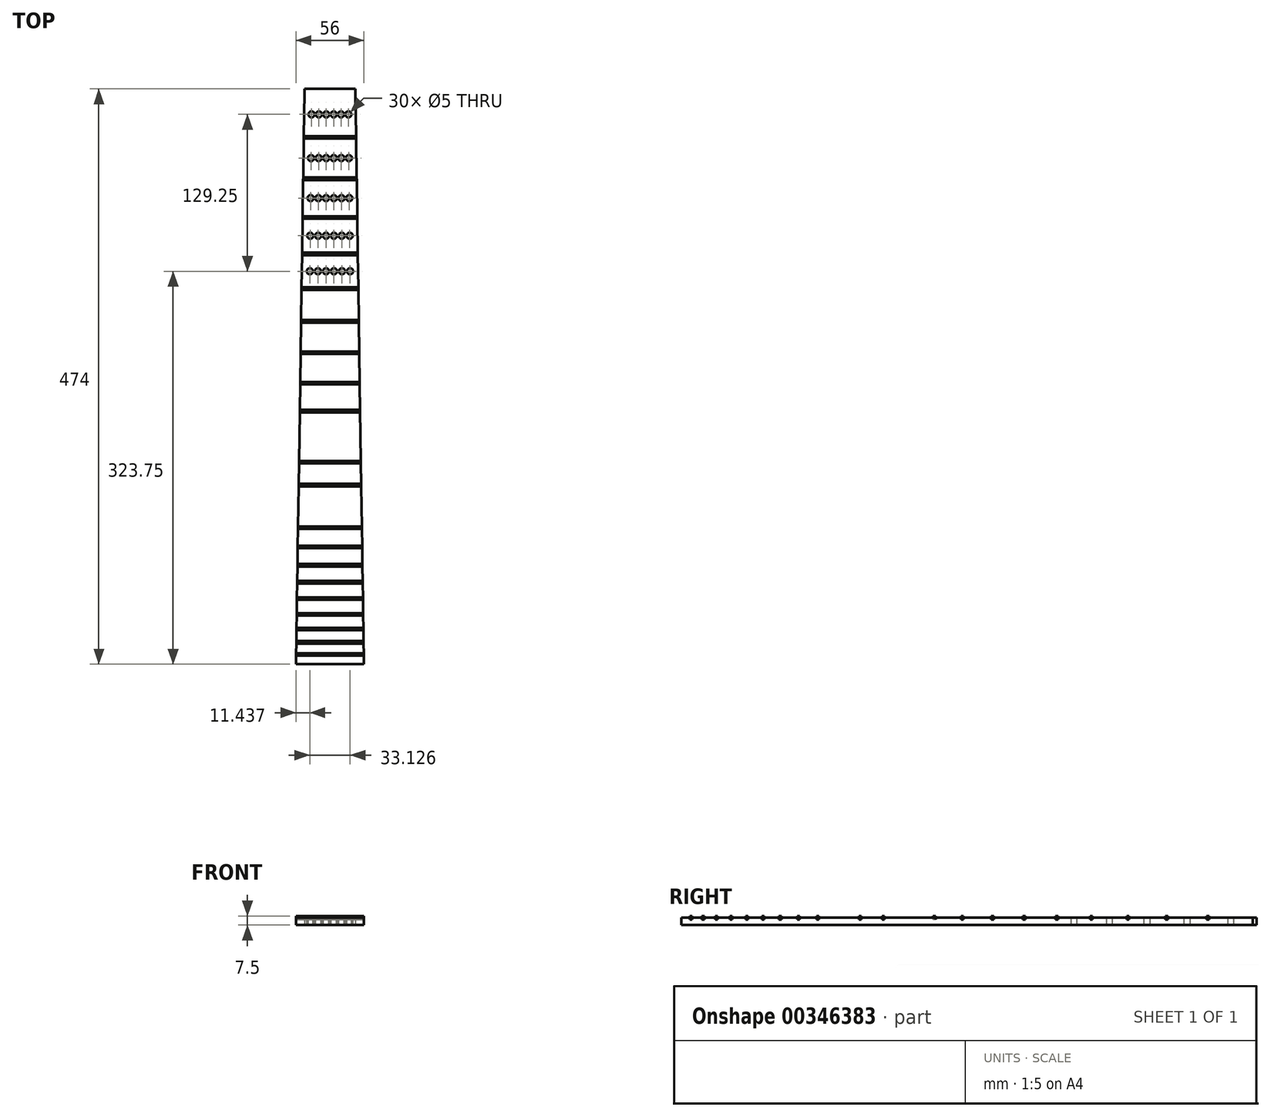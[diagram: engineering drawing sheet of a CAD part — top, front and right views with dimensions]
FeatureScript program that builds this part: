
annotation { "Feature Type Name" : "Feature", "Feature Type Description" : "" }
export const myFeature = defineFeature(function(context is Context, id is Id, definition is map)
    precondition{}
    {
        {
            var Q0;
            Q0=qCreatedBy(makeId("Top.planeOp"),FACE);
            var sketch = newSketch(context, id + "F0", { "sketchPlane" : qUnion([Q0])});
            skLineSegment(sketch, "E0", {"start": v(0, 0) * mm, "end": v(0, 471) * mm, "construction": true});
            skLineSegment(sketch, "E1", {"start": v(0, 471) * mm, "end": v(-21, 471) * mm});
            skLineSegment(sketch, "E2", {"start": v(-28, 0) * mm, "end": v(0, 0) * mm});
            skLineSegment(sketch, "E3", {"start": v(-21, 471) * mm, "end": v(-28, 0) * mm});
            skLineSegment(sketch, "E4.MirrorCS", {"start": v(0, 471) * mm, "end": v(21, 471) * mm});
            skLineSegment(sketch, "E5.MirrorCS", {"start": v(21, 471) * mm, "end": v(28, 0) * mm});
            skLineSegment(sketch, "E6.MirrorCS", {"start": v(28, 0) * mm, "end": v(0, 0) * mm});
            skLineSegment(sketch, "E7", {"start": v(-21, 471) * mm, "end": v(21, 471) * mm, "construction": true});
            skLineSegment(sketch, "E8", {"start": v(-21, 471) * mm, "end": v(-21, 474) * mm});
            skLineSegment(sketch, "E9", {"start": v(21, 471) * mm, "end": v(21, 474) * mm});
            skLineSegment(sketch, "E10", {"start": v(-21, 474) * mm, "end": v(21, 474) * mm});
            skSolve(sketch);
        }
        {
            var Q0;
            Q0 = qSketchRegion(id + "F0", true);
            extrude(context, id + "F1", {"entities" : qUnion([Q0]), "depth" : 6 * mm});
        }
        {
            var Q0;
            Q0=makeQuery(id+"F1.opExtrude","CAP_FACE",FACE,{"disambiguationData":[OSD([sQuery(id+"F0.wireOp",EDGE,"E1"),sQuery(id+"F0.wireOp",EDGE,"E2"),sQuery(id+"F0.wireOp",EDGE,"E3"),sQuery(id+"F0.wireOp",EDGE,"E4.MirrorCS"),sQuery(id+"F0.wireOp",EDGE,"E5.MirrorCS"),sQuery(id+"F0.wireOp",EDGE,"E6.MirrorCS")])],"isStart":false});
            var sketch = newSketch(context, id + "F2", { "sketchPlane" : qUnion([Q0])});
            skLineSegment(sketch, "E11", {"start": v(-21.54, 435) * mm, "end": v(21.54, 435) * mm});
            skLineSegment(sketch, "E12", {"start": v(-21.56, 433) * mm, "end": v(21.56, 433) * mm});
            skLineSegment(sketch, "E13", {"start": v(-22.04, 401) * mm, "end": v(22.04, 401) * mm});
            skLineSegment(sketch, "E14", {"start": v(-22.07, 399) * mm, "end": v(22.07, 399) * mm});
            skLineSegment(sketch, "E15", {"start": v(-22.52, 369) * mm, "end": v(22.52, 369) * mm});
            skLineSegment(sketch, "E16", {"start": v(-22.55, 367) * mm, "end": v(22.55, 367) * mm});
            skLineSegment(sketch, "E17", {"start": v(-22.96, 339) * mm, "end": v(22.96, 339) * mm});
            skLineSegment(sketch, "E18", {"start": v(-23, 337) * mm, "end": v(23, 337) * mm});
            skLineSegment(sketch, "E19", {"start": v(-23.39, 310.5) * mm, "end": v(23.39, 310.5) * mm});
            skLineSegment(sketch, "E20", {"start": v(-23.42, 308.5) * mm, "end": v(23.42, 308.5) * mm});
            skLineSegment(sketch, "E21", {"start": v(-23.79, 283.5) * mm, "end": v(23.79, 283.5) * mm});
            skLineSegment(sketch, "E22", {"start": v(-23.82, 281.5) * mm, "end": v(23.82, 281.5) * mm});
            skLineSegment(sketch, "E23", {"start": v(-24.17, 257.5) * mm, "end": v(24.17, 257.5) * mm});
            skLineSegment(sketch, "E24", {"start": v(-24.2, 255.5) * mm, "end": v(24.2, 255.5) * mm});
            skLineSegment(sketch, "E25", {"start": v(-24.54, 232.5) * mm, "end": v(24.54, 232.5) * mm});
            skLineSegment(sketch, "E26", {"start": v(-24.57, 230.5) * mm, "end": v(24.57, 230.5) * mm});
            skLineSegment(sketch, "E27", {"start": v(-24.89, 209.5) * mm, "end": v(24.89, 209.5) * mm});
            skLineSegment(sketch, "E28", {"start": v(-24.92, 207.5) * mm, "end": v(24.89, 207.5) * mm});
            skLineSegment(sketch, "E29", {"start": v(-25.21, 187.5) * mm, "end": v(25.21, 187.5) * mm});
            skLineSegment(sketch, "E30", {"start": v(-25.24, 185.5) * mm, "end": v(25.21, 185.5) * mm});
            skLineSegment(sketch, "E31", {"start": v(-25.51, 167.5) * mm, "end": v(25.51, 167.5) * mm});
            skLineSegment(sketch, "E32", {"start": v(-25.54, 165.5) * mm, "end": v(25.54, 165.5) * mm});
            skLineSegment(sketch, "E33", {"start": v(-25.8, 148.5) * mm, "end": v(25.8, 148.5) * mm});
            skLineSegment(sketch, "E34", {"start": v(-25.82, 146.5) * mm, "end": v(25.82, 146.5) * mm});
            skLineSegment(sketch, "E35", {"start": v(-26.06, 130.5) * mm, "end": v(26.06, 130.5) * mm});
            skLineSegment(sketch, "E36", {"start": v(-26.1, 128.5) * mm, "end": v(26.06, 128.5) * mm});
            skLineSegment(sketch, "E37", {"start": v(-26.31, 113.5) * mm, "end": v(26.31, 113.5) * mm});
            skLineSegment(sketch, "E38", {"start": v(-26.34, 111.5) * mm, "end": v(26.34, 111.5) * mm});
            skLineSegment(sketch, "E39", {"start": v(-26.55, 97.5) * mm, "end": v(26.55, 97.5) * mm});
            skLineSegment(sketch, "E40", {"start": v(-26.58, 95.5) * mm, "end": v(26.58, 95.5) * mm});
            skLineSegment(sketch, "E41", {"start": v(-26.77, 82.5) * mm, "end": v(26.77, 82.5) * mm});
            skLineSegment(sketch, "E42", {"start": v(-26.8, 80.5) * mm, "end": v(26.8, 80.5) * mm});
            skLineSegment(sketch, "E43", {"start": v(-26.98, 68.5) * mm, "end": v(26.98, 68.5) * mm});
            skLineSegment(sketch, "E44", {"start": v(-27.01, 66.5) * mm, "end": v(27.01, 66.5) * mm});
            skLineSegment(sketch, "E45", {"start": v(-27.18, 55) * mm, "end": v(27.18, 55) * mm});
            skLineSegment(sketch, "E46", {"start": v(-27.21, 53) * mm, "end": v(27.21, 53) * mm});
            skLineSegment(sketch, "E47", {"start": v(-27.38, 42) * mm, "end": v(27.38, 42) * mm});
            skLineSegment(sketch, "E48", {"start": v(-27.4, 40) * mm, "end": v(27.4, 40) * mm});
            skLineSegment(sketch, "E49", {"start": v(-27.55, 30) * mm, "end": v(27.55, 30) * mm});
            skLineSegment(sketch, "E50", {"start": v(-27.58, 28) * mm, "end": v(27.58, 28) * mm});
            skLineSegment(sketch, "E51", {"start": v(-27.72, 19) * mm, "end": v(27.72, 19) * mm});
            skLineSegment(sketch, "E52", {"start": v(-27.75, 17) * mm, "end": v(27.75, 17) * mm});
            skLineSegment(sketch, "E53", {"start": v(-27.87, 9) * mm, "end": v(27.87, 9) * mm});
            skLineSegment(sketch, "E54", {"start": v(-27.9, 7) * mm, "end": v(27.9, 7) * mm});
            skLineSegment(sketch, "E55", {"start": v(-21, 471) * mm, "end": v(21, 471) * mm});
            skLineSegment(sketch, "E56", {"start": v(-21.27, 453) * mm, "end": v(21.27, 453) * mm, "construction": true});
            skLineSegment(sketch, "E57", {"start": v(21, 471) * mm, "end": v(15, 471) * mm});
            skLineSegment(sketch, "E58", {"start": v(-21, 471) * mm, "end": v(-15, 471) * mm});
            skLineSegment(sketch, "E59", {"start": v(-15, 471) * mm, "end": v(-9, 471) * mm});
            skLineSegment(sketch, "E60", {"start": v(-9, 471) * mm, "end": v(-3, 471) * mm});
            skLineSegment(sketch, "E61", {"start": v(-3, 471) * mm, "end": v(3, 471) * mm});
            skLineSegment(sketch, "E62", {"start": v(3, 471) * mm, "end": v(9, 471) * mm});
            skLineSegment(sketch, "E63", {"start": v(9, 471) * mm, "end": v(15, 471) * mm});
            skLineSegment(sketch, "E64", {"start": v(-28, 0) * mm, "end": v(-20, 0) * mm});
            skLineSegment(sketch, "E65", {"start": v(-20, 0) * mm, "end": v(-12, 0) * mm});
            skLineSegment(sketch, "E66", {"start": v(-12, 0) * mm, "end": v(-4, 0) * mm});
            skLineSegment(sketch, "E67", {"start": v(-4, 0) * mm, "end": v(4, 0) * mm});
            skLineSegment(sketch, "E68", {"start": v(4, 0) * mm, "end": v(12, 0) * mm});
            skLineSegment(sketch, "E69", {"start": v(12, 0) * mm, "end": v(20, 0) * mm});
            skLineSegment(sketch, "E70", {"start": v(-15, 471) * mm, "end": v(-20, 0) * mm, "construction": true});
            skLineSegment(sketch, "E71", {"start": v(-9, 471) * mm, "end": v(-12, 0) * mm, "construction": true});
            skLineSegment(sketch, "E72", {"start": v(-3, 471) * mm, "end": v(-4, 0) * mm, "construction": true});
            skLineSegment(sketch, "E73", {"start": v(3, 471) * mm, "end": v(4, 0) * mm, "construction": true});
            skLineSegment(sketch, "E74", {"start": v(9, 471) * mm, "end": v(12, 0) * mm, "construction": true});
            skLineSegment(sketch, "E75", {"start": v(20, 0) * mm, "end": v(15, 471) * mm, "construction": true});
            skCircle(sketch, "E76", {"center": v(-15.2, 453) * mm, "radius": 2.5 * mm});
            skCircle(sketch, "E77", {"center": v(-9.11, 453) * mm, "radius": 2.5 * mm});
            skCircle(sketch, "E78", {"center": v(-3.04, 453) * mm, "radius": 2.5 * mm});
            skCircle(sketch, "E79", {"center": v(3.04, 453) * mm, "radius": 2.5 * mm});
            skCircle(sketch, "E80", {"center": v(9.11, 453) * mm, "radius": 2.5 * mm});
            skCircle(sketch, "E81", {"center": v(15.2, 453) * mm, "radius": 2.5 * mm});
            skLineSegment(sketch, "E82", {"start": v(-21.8, 417) * mm, "end": v(21.8, 417) * mm, "construction": true});
            skCircle(sketch, "E83", {"center": v(-15.57, 417) * mm, "radius": 2.5 * mm});
            skCircle(sketch, "E84", {"center": v(-9.34, 417) * mm, "radius": 2.5 * mm});
            skCircle(sketch, "E85", {"center": v(-3.11, 417) * mm, "radius": 2.5 * mm});
            skCircle(sketch, "E86", {"center": v(3.11, 417) * mm, "radius": 2.5 * mm});
            skCircle(sketch, "E87", {"center": v(9.34, 417) * mm, "radius": 2.5 * mm});
            skCircle(sketch, "E88", {"center": v(15.57, 417) * mm, "radius": 2.5 * mm});
            skLineSegment(sketch, "E89", {"start": v(-22.3, 384) * mm, "end": v(22.3, 384) * mm, "construction": true});
            skLineSegment(sketch, "E90", {"start": v(-22.75, 353) * mm, "end": v(22.75, 353) * mm, "construction": true});
            skLineSegment(sketch, "E91", {"start": v(-23.19, 323.75) * mm, "end": v(23.19, 323.75) * mm, "construction": true});
            skCircle(sketch, "E92", {"center": v(-15.92, 384) * mm, "radius": 2.5 * mm});
            skCircle(sketch, "E93", {"center": v(-9.55, 384) * mm, "radius": 2.5 * mm});
            skCircle(sketch, "E94", {"center": v(-3.18, 384) * mm, "radius": 2.5 * mm});
            skCircle(sketch, "E95", {"center": v(3.18, 384) * mm, "radius": 2.5 * mm});
            skCircle(sketch, "E96", {"center": v(9.55, 384) * mm, "radius": 2.5 * mm});
            skCircle(sketch, "E97", {"center": v(15.92, 384) * mm, "radius": 2.5 * mm});
            skCircle(sketch, "E98", {"center": v(-16.25, 353) * mm, "radius": 2.5 * mm});
            skCircle(sketch, "E99", {"center": v(-9.75, 353) * mm, "radius": 2.5 * mm});
            skCircle(sketch, "E100", {"center": v(-3.25, 353) * mm, "radius": 2.5 * mm});
            skCircle(sketch, "E101", {"center": v(3.25, 353) * mm, "radius": 2.5 * mm});
            skCircle(sketch, "E102", {"center": v(9.75, 353) * mm, "radius": 2.5 * mm});
            skCircle(sketch, "E103", {"center": v(16.25, 353) * mm, "radius": 2.5 * mm});
            skCircle(sketch, "E104", {"center": v(-16.56, 323.75) * mm, "radius": 2.5 * mm});
            skCircle(sketch, "E105", {"center": v(-9.94, 323.75) * mm, "radius": 2.5 * mm});
            skCircle(sketch, "E106", {"center": v(-3.31, 323.75) * mm, "radius": 2.5 * mm});
            skCircle(sketch, "E107", {"center": v(3.31, 323.75) * mm, "radius": 2.5 * mm});
            skCircle(sketch, "E108", {"center": v(9.94, 323.75) * mm, "radius": 2.5 * mm});
            skCircle(sketch, "E109", {"center": v(16.56, 323.75) * mm, "radius": 2.5 * mm});
            skLineSegment(sketch, "E110", {"start": v(24.89, 207.5) * mm, "end": v(24.89, 209.5) * mm});
            skLineSegment(sketch, "E111", {"start": v(-24.89, 209.5) * mm, "end": v(-24.92, 207.5) * mm});
            skSolve(sketch);
        }
        {
            var Q0;
            Q0=makeQuery(id+"F2.imprint","IMPRINT",FACE,{"disambiguationData":[TD([[makeQuery(id+"F2.imprint","IMPRINT",EDGE,{"derivedFrom":sQuery(id+"F2.wireOp",EDGE,"E81")}),1.0]])]});
            var Q1;
            Q1=makeQuery(id+"F2.imprint","IMPRINT",FACE,{"disambiguationData":[TD([[makeQuery(id+"F2.imprint","IMPRINT",EDGE,{"derivedFrom":sQuery(id+"F2.wireOp",EDGE,"E80")}),1.0]])]});
            var Q2;
            Q2=makeQuery(id+"F2.imprint","IMPRINT",FACE,{"disambiguationData":[TD([[makeQuery(id+"F2.imprint","IMPRINT",EDGE,{"derivedFrom":sQuery(id+"F2.wireOp",EDGE,"E79")}),1.0]])]});
            var Q3;
            Q3=makeQuery(id+"F2.imprint","IMPRINT",FACE,{"disambiguationData":[TD([[makeQuery(id+"F2.imprint","IMPRINT",EDGE,{"derivedFrom":sQuery(id+"F2.wireOp",EDGE,"E78")}),1.0]])]});
            var Q4;
            Q4=makeQuery(id+"F2.imprint","IMPRINT",FACE,{"disambiguationData":[TD([[makeQuery(id+"F2.imprint","IMPRINT",EDGE,{"derivedFrom":sQuery(id+"F2.wireOp",EDGE,"E77")}),1.0]])]});
            var Q5;
            Q5=makeQuery(id+"F2.imprint","IMPRINT",FACE,{"disambiguationData":[TD([[makeQuery(id+"F2.imprint","IMPRINT",EDGE,{"derivedFrom":sQuery(id+"F2.wireOp",EDGE,"E76")}),1.0]])]});
            var Q6;
            Q6=makeQuery(id+"F2.imprint","IMPRINT",FACE,{"disambiguationData":[TD([[makeQuery(id+"F2.imprint","IMPRINT",EDGE,{"derivedFrom":sQuery(id+"F2.wireOp",EDGE,"E88")}),1.0]])]});
            var Q7;
            Q7=makeQuery(id+"F2.imprint","IMPRINT",FACE,{"disambiguationData":[TD([[makeQuery(id+"F2.imprint","IMPRINT",EDGE,{"derivedFrom":sQuery(id+"F2.wireOp",EDGE,"E87")}),1.0]])]});
            var Q8;
            Q8=makeQuery(id+"F2.imprint","IMPRINT",FACE,{"disambiguationData":[TD([[makeQuery(id+"F2.imprint","IMPRINT",EDGE,{"derivedFrom":sQuery(id+"F2.wireOp",EDGE,"E86")}),1.0]])]});
            var Q9;
            Q9=makeQuery(id+"F2.imprint","IMPRINT",FACE,{"disambiguationData":[TD([[makeQuery(id+"F2.imprint","IMPRINT",EDGE,{"derivedFrom":sQuery(id+"F2.wireOp",EDGE,"E85")}),1.0]])]});
            var Q10;
            Q10=makeQuery(id+"F2.imprint","IMPRINT",FACE,{"disambiguationData":[TD([[makeQuery(id+"F2.imprint","IMPRINT",EDGE,{"derivedFrom":sQuery(id+"F2.wireOp",EDGE,"E84")}),1.0]])]});
            var Q11;
            Q11=makeQuery(id+"F2.imprint","IMPRINT",FACE,{"disambiguationData":[TD([[makeQuery(id+"F2.imprint","IMPRINT",EDGE,{"derivedFrom":sQuery(id+"F2.wireOp",EDGE,"E83")}),1.0]])]});
            var Q12;
            Q12=makeQuery(id+"F2.imprint","IMPRINT",FACE,{"disambiguationData":[TD([[makeQuery(id+"F2.imprint","IMPRINT",EDGE,{"derivedFrom":sQuery(id+"F2.wireOp",EDGE,"E97")}),1.0]])]});
            var Q13;
            Q13=makeQuery(id+"F2.imprint","IMPRINT",FACE,{"disambiguationData":[TD([[makeQuery(id+"F2.imprint","IMPRINT",EDGE,{"derivedFrom":sQuery(id+"F2.wireOp",EDGE,"E96")}),1.0]])]});
            var Q14;
            Q14=makeQuery(id+"F2.imprint","IMPRINT",FACE,{"disambiguationData":[TD([[makeQuery(id+"F2.imprint","IMPRINT",EDGE,{"derivedFrom":sQuery(id+"F2.wireOp",EDGE,"E95")}),1.0]])]});
            var Q15;
            Q15=makeQuery(id+"F2.imprint","IMPRINT",FACE,{"disambiguationData":[TD([[makeQuery(id+"F2.imprint","IMPRINT",EDGE,{"derivedFrom":sQuery(id+"F2.wireOp",EDGE,"E94")}),1.0]])]});
            var Q16;
            Q16=makeQuery(id+"F2.imprint","IMPRINT",FACE,{"disambiguationData":[TD([[makeQuery(id+"F2.imprint","IMPRINT",EDGE,{"derivedFrom":sQuery(id+"F2.wireOp",EDGE,"E93")}),1.0]])]});
            var Q17;
            Q17=makeQuery(id+"F2.imprint","IMPRINT",FACE,{"disambiguationData":[TD([[makeQuery(id+"F2.imprint","IMPRINT",EDGE,{"derivedFrom":sQuery(id+"F2.wireOp",EDGE,"E92")}),1.0]])]});
            var Q18;
            Q18=makeQuery(id+"F2.imprint","IMPRINT",FACE,{"disambiguationData":[TD([[makeQuery(id+"F2.imprint","IMPRINT",EDGE,{"derivedFrom":sQuery(id+"F2.wireOp",EDGE,"E103")}),1.0]])]});
            var Q19;
            Q19=makeQuery(id+"F2.imprint","IMPRINT",FACE,{"disambiguationData":[TD([[makeQuery(id+"F2.imprint","IMPRINT",EDGE,{"derivedFrom":sQuery(id+"F2.wireOp",EDGE,"E102")}),1.0]])]});
            var Q20;
            Q20=makeQuery(id+"F2.imprint","IMPRINT",FACE,{"disambiguationData":[TD([[makeQuery(id+"F2.imprint","IMPRINT",EDGE,{"derivedFrom":sQuery(id+"F2.wireOp",EDGE,"E101")}),1.0]])]});
            var Q21;
            Q21=makeQuery(id+"F2.imprint","IMPRINT",FACE,{"disambiguationData":[TD([[makeQuery(id+"F2.imprint","IMPRINT",EDGE,{"derivedFrom":sQuery(id+"F2.wireOp",EDGE,"E100")}),1.0]])]});
            var Q22;
            Q22=makeQuery(id+"F2.imprint","IMPRINT",FACE,{"disambiguationData":[TD([[makeQuery(id+"F2.imprint","IMPRINT",EDGE,{"derivedFrom":sQuery(id+"F2.wireOp",EDGE,"E99")}),1.0]])]});
            var Q23;
            Q23=makeQuery(id+"F2.imprint","IMPRINT",FACE,{"disambiguationData":[TD([[makeQuery(id+"F2.imprint","IMPRINT",EDGE,{"derivedFrom":sQuery(id+"F2.wireOp",EDGE,"E98")}),1.0]])]});
            var Q24;
            Q24=makeQuery(id+"F2.imprint","IMPRINT",FACE,{"disambiguationData":[TD([[makeQuery(id+"F2.imprint","IMPRINT",EDGE,{"derivedFrom":sQuery(id+"F2.wireOp",EDGE,"E109")}),1.0]])]});
            var Q25;
            Q25=makeQuery(id+"F2.imprint","IMPRINT",FACE,{"disambiguationData":[TD([[makeQuery(id+"F2.imprint","IMPRINT",EDGE,{"derivedFrom":sQuery(id+"F2.wireOp",EDGE,"E108")}),1.0]])]});
            var Q26;
            Q26=makeQuery(id+"F2.imprint","IMPRINT",FACE,{"disambiguationData":[TD([[makeQuery(id+"F2.imprint","IMPRINT",EDGE,{"derivedFrom":sQuery(id+"F2.wireOp",EDGE,"E107")}),1.0]])]});
            var Q27;
            Q27=makeQuery(id+"F2.imprint","IMPRINT",FACE,{"disambiguationData":[TD([[makeQuery(id+"F2.imprint","IMPRINT",EDGE,{"derivedFrom":sQuery(id+"F2.wireOp",EDGE,"E106")}),1.0]])]});
            var Q28;
            Q28=makeQuery(id+"F2.imprint","IMPRINT",FACE,{"disambiguationData":[TD([[makeQuery(id+"F2.imprint","IMPRINT",EDGE,{"derivedFrom":sQuery(id+"F2.wireOp",EDGE,"E105")}),1.0]])]});
            var Q29;
            Q29=makeQuery(id+"F2.imprint","IMPRINT",FACE,{"disambiguationData":[TD([[makeQuery(id+"F2.imprint","IMPRINT",EDGE,{"derivedFrom":sQuery(id+"F2.wireOp",EDGE,"E104")}),1.0]])]});
            extrude(context, id + "F3", {"entities" : qUnion([Q0, Q1, Q2, Q3, Q4, Q5, Q6, Q7, Q8, Q9, Q10, Q11, Q12, Q13, Q14, Q15, Q16, Q17, Q18, Q19, Q20, Q21, Q22, Q23, Q24, Q25, Q26, Q27, Q28, Q29]), "operationType" : NewBodyOperationType.REMOVE, "oppositeDirection" : true, "depth" : 25 * mm});
        }
        {
            var Q0;
            {var subQ0=sQuery(id+"F2.wireOp",EDGE,"E11");Q0=makeQuery(id+"F2.imprint","IMPRINT",FACE,{"disambiguationData":[TD([[makeQuery(id+"F2.imprint","IMPRINT",EDGE,{"derivedFrom":subQ0}),-1.0]])]});}
            var Q1;
            {var subQ0=sQuery(id+"F2.wireOp",EDGE,"E13");Q1=makeQuery(id+"F2.imprint","IMPRINT",FACE,{"disambiguationData":[TD([[makeQuery(id+"F2.imprint","IMPRINT",EDGE,{"derivedFrom":subQ0}),-1.0]])]});}
            var Q2;
            {var subQ0=sQuery(id+"F2.wireOp",EDGE,"E15");Q2=makeQuery(id+"F2.imprint","IMPRINT",FACE,{"disambiguationData":[TD([[makeQuery(id+"F2.imprint","IMPRINT",EDGE,{"derivedFrom":subQ0}),-1.0]])]});}
            var Q3;
            {var subQ0=sQuery(id+"F2.wireOp",EDGE,"E17");Q3=makeQuery(id+"F2.imprint","IMPRINT",FACE,{"disambiguationData":[TD([[makeQuery(id+"F2.imprint","IMPRINT",EDGE,{"derivedFrom":subQ0}),-1.0]])]});}
            var Q4;
            {var subQ0=sQuery(id+"F2.wireOp",EDGE,"E19");Q4=makeQuery(id+"F2.imprint","IMPRINT",FACE,{"disambiguationData":[TD([[makeQuery(id+"F2.imprint","IMPRINT",EDGE,{"derivedFrom":subQ0}),-1.0]])]});}
            var Q5;
            {var subQ0=sQuery(id+"F2.wireOp",EDGE,"E43");Q5=makeQuery(id+"F2.imprint","IMPRINT",FACE,{"disambiguationData":[TD([[makeQuery(id+"F2.imprint","IMPRINT",EDGE,{"derivedFrom":subQ0}),-1.0]])]});}
            var Q6;
            {var subQ0=sQuery(id+"F2.wireOp",EDGE,"E45");Q6=makeQuery(id+"F2.imprint","IMPRINT",FACE,{"disambiguationData":[TD([[makeQuery(id+"F2.imprint","IMPRINT",EDGE,{"derivedFrom":subQ0}),-1.0]])]});}
            var Q7;
            {var subQ0=sQuery(id+"F2.wireOp",EDGE,"E47");Q7=makeQuery(id+"F2.imprint","IMPRINT",FACE,{"disambiguationData":[TD([[makeQuery(id+"F2.imprint","IMPRINT",EDGE,{"derivedFrom":subQ0}),-1.0]])]});}
            var Q8;
            {var subQ0=sQuery(id+"F2.wireOp",EDGE,"E49");Q8=makeQuery(id+"F2.imprint","IMPRINT",FACE,{"disambiguationData":[TD([[makeQuery(id+"F2.imprint","IMPRINT",EDGE,{"derivedFrom":subQ0}),-1.0]])]});}
            var Q9;
            {var subQ0=sQuery(id+"F2.wireOp",EDGE,"E51");Q9=makeQuery(id+"F2.imprint","IMPRINT",FACE,{"disambiguationData":[TD([[makeQuery(id+"F2.imprint","IMPRINT",EDGE,{"derivedFrom":subQ0}),-1.0]])]});}
            var Q10;
            {var subQ0=sQuery(id+"F2.wireOp",EDGE,"E53");Q10=makeQuery(id+"F2.imprint","IMPRINT",FACE,{"disambiguationData":[TD([[makeQuery(id+"F2.imprint","IMPRINT",EDGE,{"derivedFrom":subQ0}),-1.0]])]});}
            var Q11;
            {var subQ0=sQuery(id+"F2.wireOp",EDGE,"E39");Q11=makeQuery(id+"F2.imprint","IMPRINT",FACE,{"disambiguationData":[TD([[makeQuery(id+"F2.imprint","IMPRINT",EDGE,{"derivedFrom":subQ0}),-1.0]])]});}
            var Q12;
            {var subQ0=sQuery(id+"F2.wireOp",EDGE,"E37");Q12=makeQuery(id+"F2.imprint","IMPRINT",FACE,{"disambiguationData":[TD([[makeQuery(id+"F2.imprint","IMPRINT",EDGE,{"derivedFrom":subQ0}),-1.0]])]});}
            var Q13;
            {var subQ0=sQuery(id+"F2.wireOp",EDGE,"E41");Q13=makeQuery(id+"F2.imprint","IMPRINT",FACE,{"disambiguationData":[TD([[makeQuery(id+"F2.imprint","IMPRINT",EDGE,{"derivedFrom":subQ0}),-1.0]])]});}
            var Q14;
            {var subQ0=sQuery(id+"F2.wireOp",EDGE,"E33");Q14=makeQuery(id+"F2.imprint","IMPRINT",FACE,{"disambiguationData":[TD([[makeQuery(id+"F2.imprint","IMPRINT",EDGE,{"derivedFrom":subQ0}),-1.0]])]});}
            var Q15;
            {var subQ0=sQuery(id+"F2.wireOp",EDGE,"E31");Q15=makeQuery(id+"F2.imprint","IMPRINT",FACE,{"disambiguationData":[TD([[makeQuery(id+"F2.imprint","IMPRINT",EDGE,{"derivedFrom":subQ0}),-1.0]])]});}
            var Q16;
            {var subQ0=sQuery(id+"F2.wireOp",EDGE,"E23");Q16=makeQuery(id+"F2.imprint","IMPRINT",FACE,{"disambiguationData":[TD([[makeQuery(id+"F2.imprint","IMPRINT",EDGE,{"derivedFrom":subQ0}),-1.0]])]});}
            var Q17;
            {var subQ0=sQuery(id+"F2.wireOp",EDGE,"E25");Q17=makeQuery(id+"F2.imprint","IMPRINT",FACE,{"disambiguationData":[TD([[makeQuery(id+"F2.imprint","IMPRINT",EDGE,{"derivedFrom":subQ0}),-1.0]])]});}
            var Q18;
            {var subQ0=sQuery(id+"F2.wireOp",EDGE,"E21");Q18=makeQuery(id+"F2.imprint","IMPRINT",FACE,{"disambiguationData":[TD([[makeQuery(id+"F2.imprint","IMPRINT",EDGE,{"derivedFrom":subQ0}),-1.0]])]});}
            var Q19;
            Q19=makeQuery(id+"F2.imprint","IMPRINT",FACE,{"disambiguationData":[TD([[makeQuery(id+"F2.imprint","IMPRINT",EDGE,{"derivedFrom":sQuery(id+"F2.wireOp",EDGE,"E27")}),-1.0]])]});
            extrude(context, id + "F4", {"entities" : qUnion([Q0, Q1, Q2, Q3, Q4, Q5, Q6, Q7, Q8, Q9, Q10, Q11, Q12, Q13, Q14, Q15, Q16, Q17, Q18, Q19]), "endBound" : BoundingType.SYMMETRIC, "depth" : 3 * mm});
        }
    });
